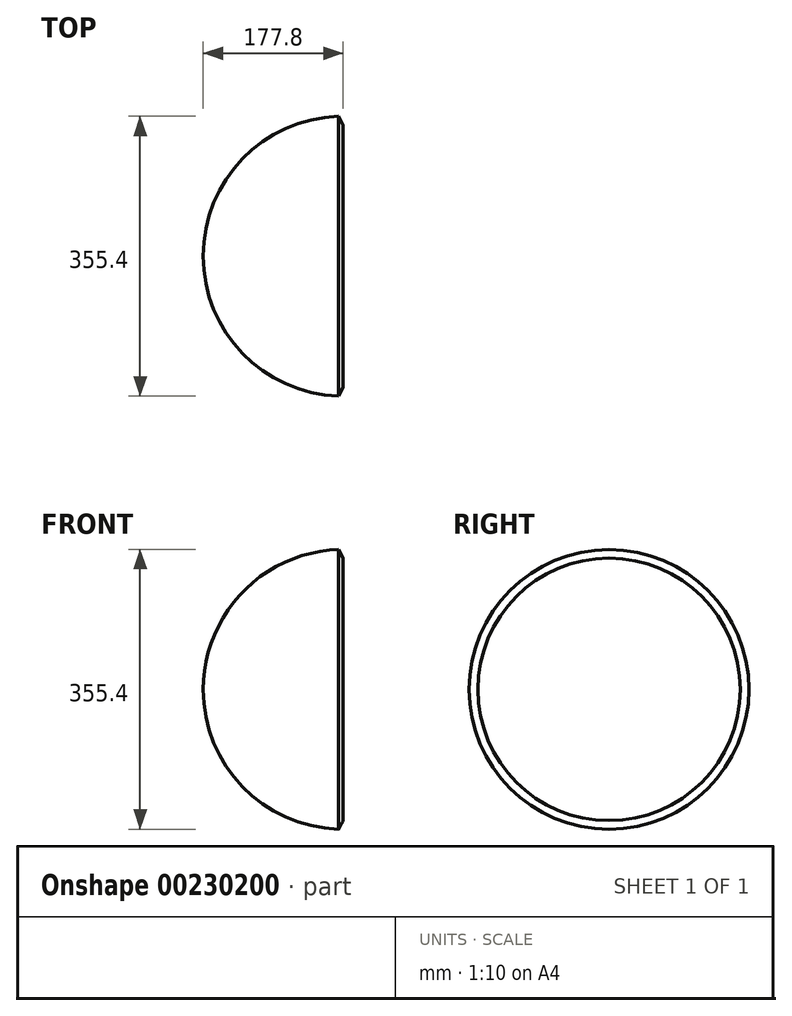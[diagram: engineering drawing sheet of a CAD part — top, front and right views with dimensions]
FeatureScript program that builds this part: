
annotation { "Feature Type Name" : "Feature", "Feature Type Description" : "" }
export const myFeature = defineFeature(function(context is Context, id is Id, definition is map)
    precondition{}
    {
        {
            var Q0;
            Q0=qCreatedBy(makeId("Front.planeOp"),FACE);
            var sketch = newSketch(context, id + "F0", { "sketchPlane" : qUnion([Q0])});
            skArc(sketch, "E0", {"start": v(-5.86, 177.7) * mm, "mid": v(-127.78, 123.64) * mm, "end": v(-177.8, 0) * mm});
            skArc(sketch, "E1", {"start": v(0, 166.69) * mm, "mid": v(-117.87, 117.87) * mm, "end": v(-166.69, 0) * mm});
            skLineSegment(sketch, "E2", {"start": v(0, 166.69) * mm, "end": v(0, 0) * mm});
            skLineSegment(sketch, "E3", {"start": v(0, 166.69) * mm, "end": v(-5.86, 177.7) * mm});
            skPoint(sketch, "E4.orphan", {"position": v(0, 177.8) * mm});
            skLineSegment(sketch, "E5", {"start": v(0, 0) * mm, "end": v(-177.8, 0) * mm});
            skSolve(sketch);
        }
        {
            var Q0;
            Q0 = qSketchRegion(id + "F0", true);
            var Q1;
            Q1=sQuery(id+"F0.wireOp",EDGE,"E5");
            revolve(context, id + "F1", {"entities" : qUnion([Q0]), "axis" : qUnion([Q1]), "revolveType" : RevolveType.FULL});
        }
    });
